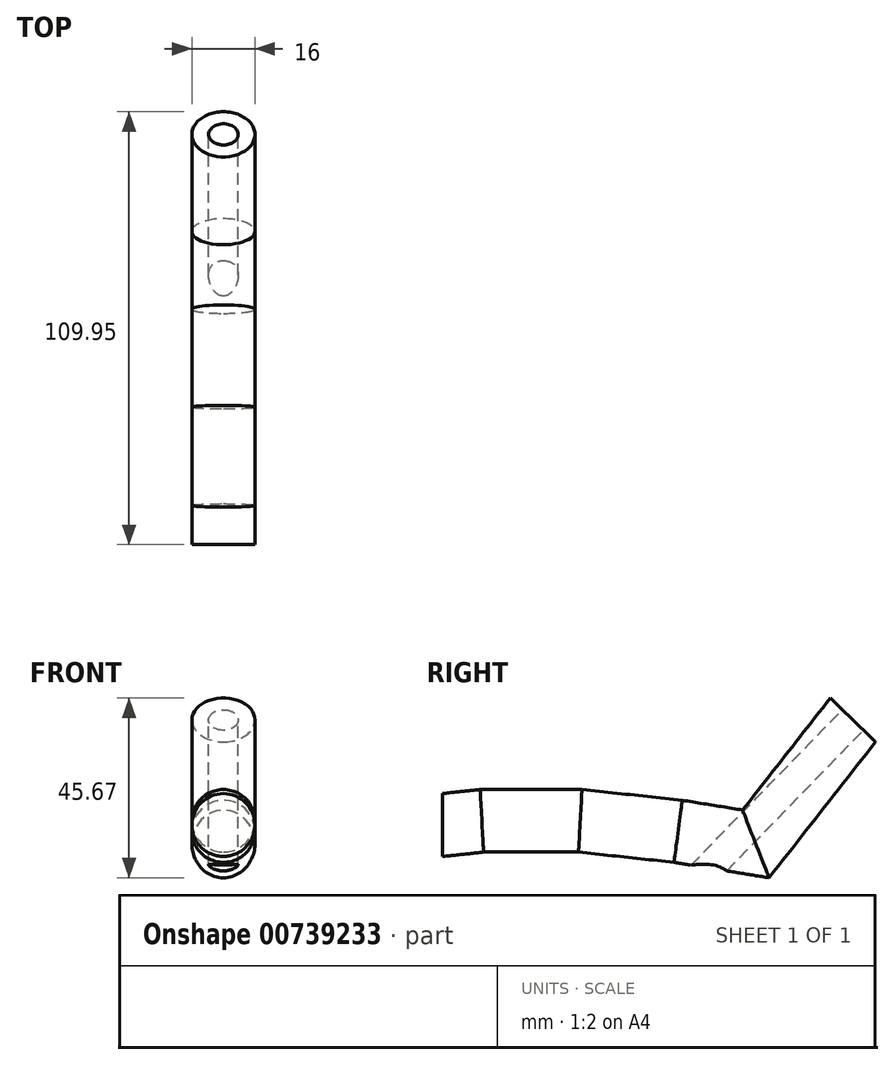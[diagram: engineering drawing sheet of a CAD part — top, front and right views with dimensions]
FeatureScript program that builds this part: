
annotation { "Feature Type Name" : "Feature", "Feature Type Description" : "" }
export const myFeature = defineFeature(function(context is Context, id is Id, definition is map)
    precondition{}
    {
        {
            var Q0;
            Q0=qCreatedBy(makeId("Front.planeOp"),FACE);
            var sketch = newSketch(context, id + "F0", { "sketchPlane" : qUnion([Q0])});
            skCircle(sketch, "E0", {"center": v(0, 0) * mm, "radius": 8 * mm});
            skSolve(sketch);
        }
        {
            var Q0;
            Q0=qCreatedBy(makeId("Right.planeOp"),FACE);
            var sketch = newSketch(context, id + "F1", { "sketchPlane" : qUnion([Q0])});
            skLineSegment(sketch, "E1", {"start": v(0, 0) * mm, "end": v(9.94, 1.07) * mm});
            skLineSegment(sketch, "E2", {"start": v(9.94, 1.07) * mm, "end": v(34.94, 1.07) * mm});
            skLineSegment(sketch, "E3", {"start": v(34.94, 1.07) * mm, "end": v(59.8, -1.6) * mm});
            skLineSegment(sketch, "E4", {"start": v(59.8, -1.6) * mm, "end": v(79.54, -4.8) * mm});
            skLineSegment(sketch, "E5", {"start": v(79.54, -4.8) * mm, "end": v(104.22, 26.68) * mm});
            skSolve(sketch);
        }
        {
            var Q0;
            Q0=makeQuery(id+"F0.imprint","IMPRINT",FACE,{"disambiguationData":[TD([[makeQuery(id+"F0.imprint","IMPRINT",EDGE,{"derivedFrom":sQuery(id+"F0.wireOp",EDGE,"E0")}),1.0]])]});
            var Q1;
            Q1 = qConstructionFilter(qBodyType(qCreatedBy(id + "F1" ,EDGE), BodyType.WIRE), ConstructionObject.NO);
            sweep(context, id + "F2", {"profiles" : qUnion([Q0]), "path" : qUnion([Q1])});
        }
        {
            var Q0;
            Q0=makeQuery(id+"F2.opSweep","CAP_FACE",FACE,{"disambiguationData":[OSD([sQuery(id+"F0.wireOp",EDGE,"E0"),sQuery(id+"F1.wireOp",VERTEX,"E5.end")])],"isStart":false});
            var sketch = newSketch(context, id + "F3", { "sketchPlane" : qUnion([Q0])});
            skCircle(sketch, "E6", {"center": v(0, 56.1) * mm, "radius": 3.75 * mm});
            skSolve(sketch);
        }
        {
            var Q0;
            Q0 = qSketchRegion(id + "F3", true);
            extrude(context, id + "F4", {"entities" : qUnion([Q0]), "operationType" : NewBodyOperationType.REMOVE, "oppositeDirection" : true, "depth" : 60 * mm, "offsetDistance" : 25.4 * mm});
        }
    });
